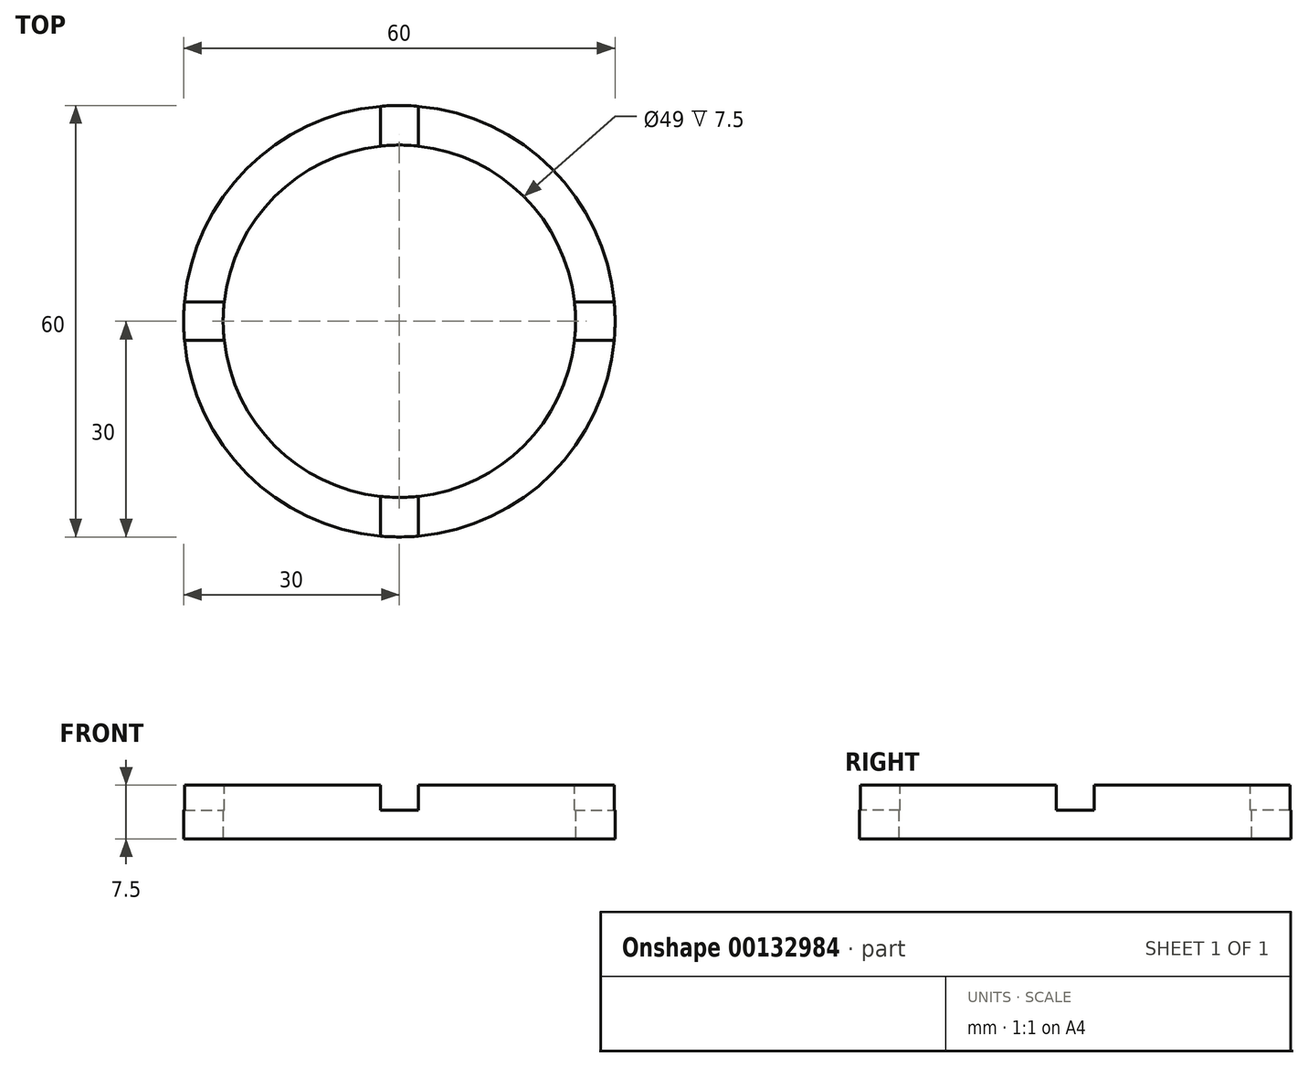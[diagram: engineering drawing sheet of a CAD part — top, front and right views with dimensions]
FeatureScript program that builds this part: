
annotation { "Feature Type Name" : "Feature", "Feature Type Description" : "" }
export const myFeature = defineFeature(function(context is Context, id is Id, definition is map)
    precondition{}
    {
        {
            var Q0;
            Q0=qCreatedBy(makeId("Top.planeOp"),FACE);
            var sketch = newSketch(context, id + "F0", { "sketchPlane" : qUnion([Q0])});
            skCircle(sketch, "E0", {"center": v(0, 0) * mm, "radius": 24.5 * mm});
            skCircle(sketch, "E1", {"center": v(0, 0) * mm, "radius": 30 * mm});
            skSolve(sketch);
        }
        {
            var Q0;
            Q0=makeQuery(id+"F0.imprint","IMPRINT",FACE,{"disambiguationData":[TD([[makeQuery(id+"F0.imprint","IMPRINT",EDGE,{"derivedFrom":sQuery(id+"F0.wireOp",EDGE,"E0")}),-1.0]])]});
            extrude(context, id + "F1", {"entities" : qUnion([Q0]), "depth" : 7.5 * mm});
        }
        {
            var Q0;
            Q0=makeQuery(id+"F1.opExtrude","CAP_FACE",FACE,{"disambiguationData":[OSD([sQuery(id+"F0.wireOp",EDGE,"E0"),sQuery(id+"F0.wireOp",EDGE,"E1")])],"isStart":false});
            var sketch = newSketch(context, id + "F2", { "sketchPlane" : qUnion([Q0])});
            skLineSegment(sketch, "E2.bottom", {"start": v(-2.65, 32.58) * mm, "end": v(2.65, 32.58) * mm});
            skLineSegment(sketch, "E2.top", {"start": v(-2.65, 20.66) * mm, "end": v(2.65, 20.66) * mm});
            skLineSegment(sketch, "E2.left", {"start": v(-2.65, 32.58) * mm, "end": v(-2.65, 20.66) * mm});
            skLineSegment(sketch, "E2.right", {"start": v(2.65, 32.58) * mm, "end": v(2.65, 20.66) * mm});
            skLineSegment(sketch, "E3.bottom", {"start": v(23.26, 2.65) * mm, "end": v(32.31, 2.65) * mm});
            skLineSegment(sketch, "E3.top", {"start": v(23.26, -2.65) * mm, "end": v(32.31, -2.65) * mm});
            skLineSegment(sketch, "E3.left", {"start": v(23.26, 2.65) * mm, "end": v(23.26, -2.65) * mm});
            skLineSegment(sketch, "E3.right", {"start": v(32.31, 2.65) * mm, "end": v(32.31, -2.65) * mm});
            skLineSegment(sketch, "E4.bottom", {"start": v(-2.65, -22.26) * mm, "end": v(2.65, -22.26) * mm});
            skLineSegment(sketch, "E4.top", {"start": v(-2.65, -33.35) * mm, "end": v(2.65, -33.35) * mm});
            skLineSegment(sketch, "E4.left", {"start": v(-2.65, -22.26) * mm, "end": v(-2.65, -33.35) * mm});
            skLineSegment(sketch, "E4.right", {"start": v(2.65, -22.26) * mm, "end": v(2.65, -33.35) * mm});
            skLineSegment(sketch, "E5.bottom", {"start": v(-32.33, 2.65) * mm, "end": v(-21.3, 2.65) * mm});
            skLineSegment(sketch, "E5.top", {"start": v(-32.33, -2.65) * mm, "end": v(-21.3, -2.65) * mm});
            skLineSegment(sketch, "E5.left", {"start": v(-32.33, 2.65) * mm, "end": v(-32.33, -2.65) * mm});
            skLineSegment(sketch, "E5.right", {"start": v(-21.3, 2.65) * mm, "end": v(-21.3, -2.65) * mm});
            skSolve(sketch);
        }
        {
            var Q0;
            {var subQ0=sQuery(id+"F2.wireOp",EDGE,"E4.left");var subQ1=makeQuery(id+"F1.opExtrude","CAP_EDGE",EDGE,{"disambiguationData":[OSD([sQuery(id+"F0.wireOp",EDGE,"E1")])],"isStart":false});var subQ2=makeQuery(id+"F2.imprint","INTERSECT",VERTEX,{"derivedFrom":[subQ1,subQ0]});Q0=makeQuery(id+"F2.imprint","IMPRINT",FACE,{"disambiguationData":[TD([[makeQuery(id+"F2.imprint","IMPRINT",EDGE,{"disambiguationData":[TD([[subQ2,1.0]])],"derivedFrom":subQ0}),1.0]])]});}
            var Q1;
            {var subQ0=sQuery(id+"F2.wireOp",EDGE,"E3.bottom");var subQ1=makeQuery(id+"F1.opExtrude","CAP_EDGE",EDGE,{"disambiguationData":[OSD([sQuery(id+"F0.wireOp",EDGE,"E1")])],"isStart":false});var subQ2=makeQuery(id+"F2.imprint","INTERSECT",VERTEX,{"derivedFrom":[subQ1,subQ0]});Q1=makeQuery(id+"F2.imprint","IMPRINT",FACE,{"disambiguationData":[TD([[makeQuery(id+"F2.imprint","IMPRINT",EDGE,{"disambiguationData":[TD([[subQ2,1.0]])],"derivedFrom":subQ0}),-1.0]])]});}
            var Q2;
            {var subQ0=sQuery(id+"F2.wireOp",EDGE,"E2.left");var subQ1=makeQuery(id+"F1.opExtrude","CAP_EDGE",EDGE,{"disambiguationData":[OSD([sQuery(id+"F0.wireOp",EDGE,"E1")])],"isStart":false});var subQ2=makeQuery(id+"F2.imprint","INTERSECT",VERTEX,{"derivedFrom":[subQ1,subQ0]});Q2=makeQuery(id+"F2.imprint","IMPRINT",FACE,{"disambiguationData":[TD([[makeQuery(id+"F2.imprint","IMPRINT",EDGE,{"disambiguationData":[TD([[subQ2,-1.0]])],"derivedFrom":subQ0}),1.0]])]});}
            var Q3;
            {var subQ0=sQuery(id+"F2.wireOp",EDGE,"E5.bottom");var subQ1=makeQuery(id+"F1.opExtrude","CAP_EDGE",EDGE,{"disambiguationData":[OSD([sQuery(id+"F0.wireOp",EDGE,"E1")])],"isStart":false});var subQ2=makeQuery(id+"F2.imprint","INTERSECT",VERTEX,{"derivedFrom":[subQ1,subQ0]});Q3=makeQuery(id+"F2.imprint","IMPRINT",FACE,{"disambiguationData":[TD([[makeQuery(id+"F2.imprint","IMPRINT",EDGE,{"disambiguationData":[TD([[subQ2,-1.0]])],"derivedFrom":subQ0}),-1.0]])]});}
            extrude(context, id + "F3", {"entities" : qUnion([Q0, Q1, Q2, Q3]), "operationType" : NewBodyOperationType.REMOVE, "oppositeDirection" : true, "depth" : 3.5 * mm});
        }
    });
